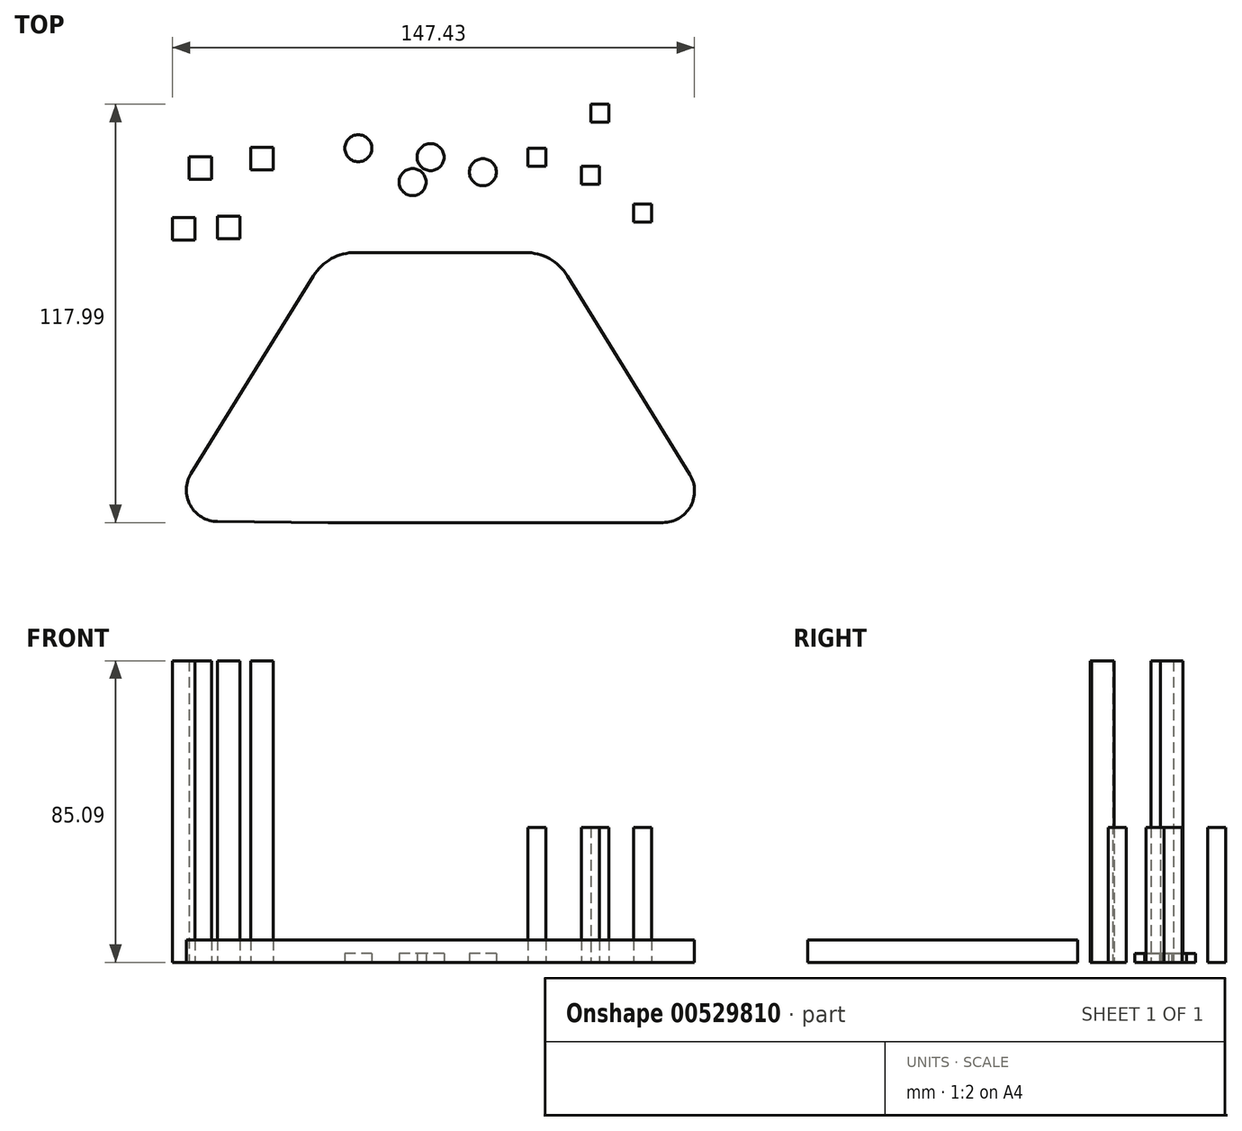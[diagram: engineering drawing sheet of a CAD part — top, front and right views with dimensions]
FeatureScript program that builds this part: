
annotation { "Feature Type Name" : "Feature", "Feature Type Description" : "" }
export const myFeature = defineFeature(function(context is Context, id is Id, definition is map)
    precondition{}
    {
        {
            var Q0;
            Q0=qCreatedBy(makeId("Top.planeOp"),FACE);
            var sketch = newSketch(context, id + "F0", { "sketchPlane" : qUnion([Q0])});
            skLineSegment(sketch, "E0.bottom", {"start": v(23.95, 38.1) * mm, "end": v(-23.97, 38.1) * mm});
            skLineSegment(sketch, "E0.top", {"start": v(31.75, -38.1) * mm, "end": v(-31.75, -38.1) * mm});
            skLineSegment(sketch, "E0.left", {"start": v(31.75, 38.1) * mm, "end": v(31.75, -38.1) * mm});
            skLineSegment(sketch, "E0.right", {"start": v(-31.75, 38.1) * mm, "end": v(-31.75, -38.1) * mm});
            skPoint(sketch, "E0.middle", {"position": v(0, 0) * mm});
            skLineSegment(sketch, "E1", {"start": v(-35.85, 31.5) * mm, "end": v(-70.4, -24.26) * mm});
            skLineSegment(sketch, "E2", {"start": v(-62.93, -37.83) * mm, "end": v(-31.75, -38.1) * mm});
            skLineSegment(sketch, "E3", {"start": v(31.75, -38.1) * mm, "end": v(62.83, -38.1) * mm});
            skLineSegment(sketch, "E4", {"start": v(70.39, -24.56) * mm, "end": v(35.84, 31.46) * mm});
            skPoint(sketch, "E5.visualSharp", {"position": v(-78.74, -37.7) * mm});
            skArc(sketch, "E5.filletArc", {"start": v(-70.4, -24.26) * mm, "mid": v(-70.64, -33.23) * mm, "end": v(-62.93, -37.83) * mm});
            skPoint(sketch, "E6.visualSharp", {"position": v(78.74, -38.1) * mm});
            skArc(sketch, "E6.filletArc", {"start": v(62.83, -38.1) * mm, "mid": v(70.58, -33.55) * mm, "end": v(70.39, -24.56) * mm});
            skPoint(sketch, "E7.visualSharp", {"position": v(-31.75, 38.1) * mm});
            skArc(sketch, "E7.filletArc", {"start": v(-23.97, 38.1) * mm, "mid": v(-30.77, 36.34) * mm, "end": v(-35.85, 31.5) * mm});
            skPoint(sketch, "E8.visualSharp", {"position": v(31.75, 38.1) * mm});
            skArc(sketch, "E8.filletArc", {"start": v(35.84, 31.46) * mm, "mid": v(30.76, 36.33) * mm, "end": v(23.95, 38.1) * mm});
            skSolve(sketch);
        }
        {
            var Q0;
            {var subQ7=sQuery(id+"F0.wireOp",EDGE,"E0.bottom");Q0=makeQuery(id+"F0.imprint","IMPRINT",FACE,{"disambiguationData":[TD([[makeQuery(id+"F0.imprint","IMPRINT",EDGE,{"derivedFrom":subQ7}),1.0]])]});}
            var Q1;
            {var subQ1=sQuery(id+"F0.wireOp",EDGE,"E1");Q1=makeQuery(id+"F0.imprint","IMPRINT",FACE,{"disambiguationData":[TD([[makeQuery(id+"F0.imprint","IMPRINT",EDGE,{"derivedFrom":subQ1}),1.0]])]});}
            var Q2;
            {var subQ0=sQuery(id+"F0.wireOp",EDGE,"E3");Q2=makeQuery(id+"F0.imprint","IMPRINT",FACE,{"disambiguationData":[TD([[makeQuery(id+"F0.imprint","IMPRINT",EDGE,{"derivedFrom":subQ0}),1.0]])]});}
            extrude(context, id + "F1", {"entities" : qUnion([Q0, Q1, Q2]), "depth" : 6.35 * mm, "offsetDistance" : 25.4 * mm});
        }
        {
            var Q0;
            Q0=qCreatedBy(makeId("Top.planeOp"),FACE);
            var sketch = newSketch(context, id + "F2", { "sketchPlane" : qUnion([Q0])});
            skLineSegment(sketch, "E9.bottom", {"start": v(-64.56, 58.8) * mm, "end": v(-70.91, 58.8) * mm});
            skLineSegment(sketch, "E9.top", {"start": v(-64.56, 65.14) * mm, "end": v(-70.91, 65.14) * mm});
            skLineSegment(sketch, "E9.left", {"start": v(-64.56, 58.8) * mm, "end": v(-64.56, 65.14) * mm});
            skLineSegment(sketch, "E9.right", {"start": v(-70.91, 58.8) * mm, "end": v(-70.91, 65.14) * mm});
            skPoint(sketch, "E9.middle", {"position": v(-67.74, 61.97) * mm});
            skLineSegment(sketch, "E10.bottom", {"start": v(-69.37, 41.56) * mm, "end": v(-75.72, 41.56) * mm});
            skLineSegment(sketch, "E10.top", {"start": v(-69.37, 47.9) * mm, "end": v(-75.72, 47.9) * mm});
            skLineSegment(sketch, "E10.left", {"start": v(-69.37, 41.56) * mm, "end": v(-69.37, 47.9) * mm});
            skLineSegment(sketch, "E10.right", {"start": v(-75.72, 41.56) * mm, "end": v(-75.72, 47.9) * mm});
            skPoint(sketch, "E10.middle", {"position": v(-72.55, 44.73) * mm});
            skLineSegment(sketch, "E11.bottom", {"start": v(-47.24, 61.38) * mm, "end": v(-53.6, 61.38) * mm});
            skLineSegment(sketch, "E11.top", {"start": v(-47.24, 67.73) * mm, "end": v(-53.6, 67.73) * mm});
            skLineSegment(sketch, "E11.left", {"start": v(-47.24, 61.38) * mm, "end": v(-47.24, 67.73) * mm});
            skLineSegment(sketch, "E11.right", {"start": v(-53.6, 61.38) * mm, "end": v(-53.6, 67.73) * mm});
            skPoint(sketch, "E11.middle", {"position": v(-50.42, 64.56) * mm});
            skLineSegment(sketch, "E12.bottom", {"start": v(-56.67, 42.03) * mm, "end": v(-63.02, 42.03) * mm});
            skLineSegment(sketch, "E12.top", {"start": v(-56.67, 48.38) * mm, "end": v(-63.02, 48.38) * mm});
            skLineSegment(sketch, "E12.left", {"start": v(-56.67, 42.03) * mm, "end": v(-56.67, 48.38) * mm});
            skLineSegment(sketch, "E12.right", {"start": v(-63.02, 42.03) * mm, "end": v(-63.02, 48.38) * mm});
            skPoint(sketch, "E12.middle", {"position": v(-59.85, 45.2) * mm});
            skSolve(sketch);
        }
        {
            var Q0;
            Q0 = qSketchRegion(id + "F2", true);
            extrude(context, id + "F3", {"entities" : qUnion([Q0]), "depth" : 85.1 * mm, "offsetDistance" : 25.4 * mm});
        }
        {
            var Q0;
            Q0=qCreatedBy(makeId("Top.planeOp"),FACE);
            var sketch = newSketch(context, id + "F4", { "sketchPlane" : qUnion([Q0])});
            skLineSegment(sketch, "E13.bottom", {"start": v(29.7, 62.38) * mm, "end": v(24.63, 62.38) * mm});
            skLineSegment(sketch, "E13.top", {"start": v(29.7, 67.46) * mm, "end": v(24.63, 67.46) * mm});
            skLineSegment(sketch, "E13.left", {"start": v(29.7, 62.38) * mm, "end": v(29.7, 67.46) * mm});
            skLineSegment(sketch, "E13.right", {"start": v(24.63, 62.38) * mm, "end": v(24.63, 67.46) * mm});
            skPoint(sketch, "E13.middle", {"position": v(27.17, 64.92) * mm});
            skLineSegment(sketch, "E14.bottom", {"start": v(47.5, 74.8) * mm, "end": v(42.42, 74.8) * mm});
            skLineSegment(sketch, "E14.top", {"start": v(47.5, 79.89) * mm, "end": v(42.42, 79.89) * mm});
            skLineSegment(sketch, "E14.left", {"start": v(47.5, 74.8) * mm, "end": v(47.5, 79.89) * mm});
            skLineSegment(sketch, "E14.right", {"start": v(42.42, 74.8) * mm, "end": v(42.42, 79.89) * mm});
            skPoint(sketch, "E14.middle", {"position": v(44.96, 77.35) * mm});
            skLineSegment(sketch, "E15.bottom", {"start": v(44.84, 57.36) * mm, "end": v(39.76, 57.36) * mm});
            skLineSegment(sketch, "E15.top", {"start": v(44.84, 62.44) * mm, "end": v(39.76, 62.44) * mm});
            skLineSegment(sketch, "E15.left", {"start": v(44.84, 57.36) * mm, "end": v(44.84, 62.44) * mm});
            skLineSegment(sketch, "E15.right", {"start": v(39.76, 57.36) * mm, "end": v(39.76, 62.44) * mm});
            skPoint(sketch, "E15.middle", {"position": v(42.3, 59.9) * mm});
            skLineSegment(sketch, "E16.bottom", {"start": v(59.63, 46.7) * mm, "end": v(54.55, 46.7) * mm});
            skLineSegment(sketch, "E16.top", {"start": v(59.63, 51.79) * mm, "end": v(54.55, 51.79) * mm});
            skLineSegment(sketch, "E16.left", {"start": v(59.63, 46.7) * mm, "end": v(59.63, 51.79) * mm});
            skLineSegment(sketch, "E16.right", {"start": v(54.55, 46.7) * mm, "end": v(54.55, 51.79) * mm});
            skPoint(sketch, "E16.middle", {"position": v(57.09, 49.25) * mm});
            skSolve(sketch);
        }
        {
            var Q0;
            Q0 = qSketchRegion(id + "F4", true);
            extrude(context, id + "F5", {"entities" : qUnion([Q0]), "depth" : 38.1 * mm, "offsetDistance" : 25.4 * mm});
        }
        {
            var Q0;
            Q0=qCreatedBy(makeId("Top.planeOp"),FACE);
            var sketch = newSketch(context, id + "F6", { "sketchPlane" : qUnion([Q0])});
            skCircle(sketch, "E17", {"center": v(-2.8, 65) * mm, "radius": 3.81 * mm});
            skCircle(sketch, "E18", {"center": v(11.97, 60.75) * mm, "radius": 3.81 * mm});
            skCircle(sketch, "E19", {"center": v(-7.87, 57.93) * mm, "radius": 3.81 * mm});
            skCircle(sketch, "E20", {"center": v(-23.19, 67.5) * mm, "radius": 3.81 * mm});
            skSolve(sketch);
        }
        {
            var Q0;
            Q0 = qConstructionFilter(qBodyType(qCreatedBy(id + "F6" ,EDGE), BodyType.WIRE), ConstructionObject.NO);
            extrude(context, id + "F7", {"bodyType" : ToolBodyType.SURFACE, "surfaceEntities" : qUnion([Q0]), "depth" : 2.54 * mm, "offsetDistance" : 25.4 * mm});
        }
        {
            var Q0;
            Q0 = qSketchRegion(id + "F6", true);
            extrude(context, id + "F8", {"entities" : qUnion([Q0]), "depth" : 2.54 * mm, "offsetDistance" : 25.4 * mm});
        }
    });
